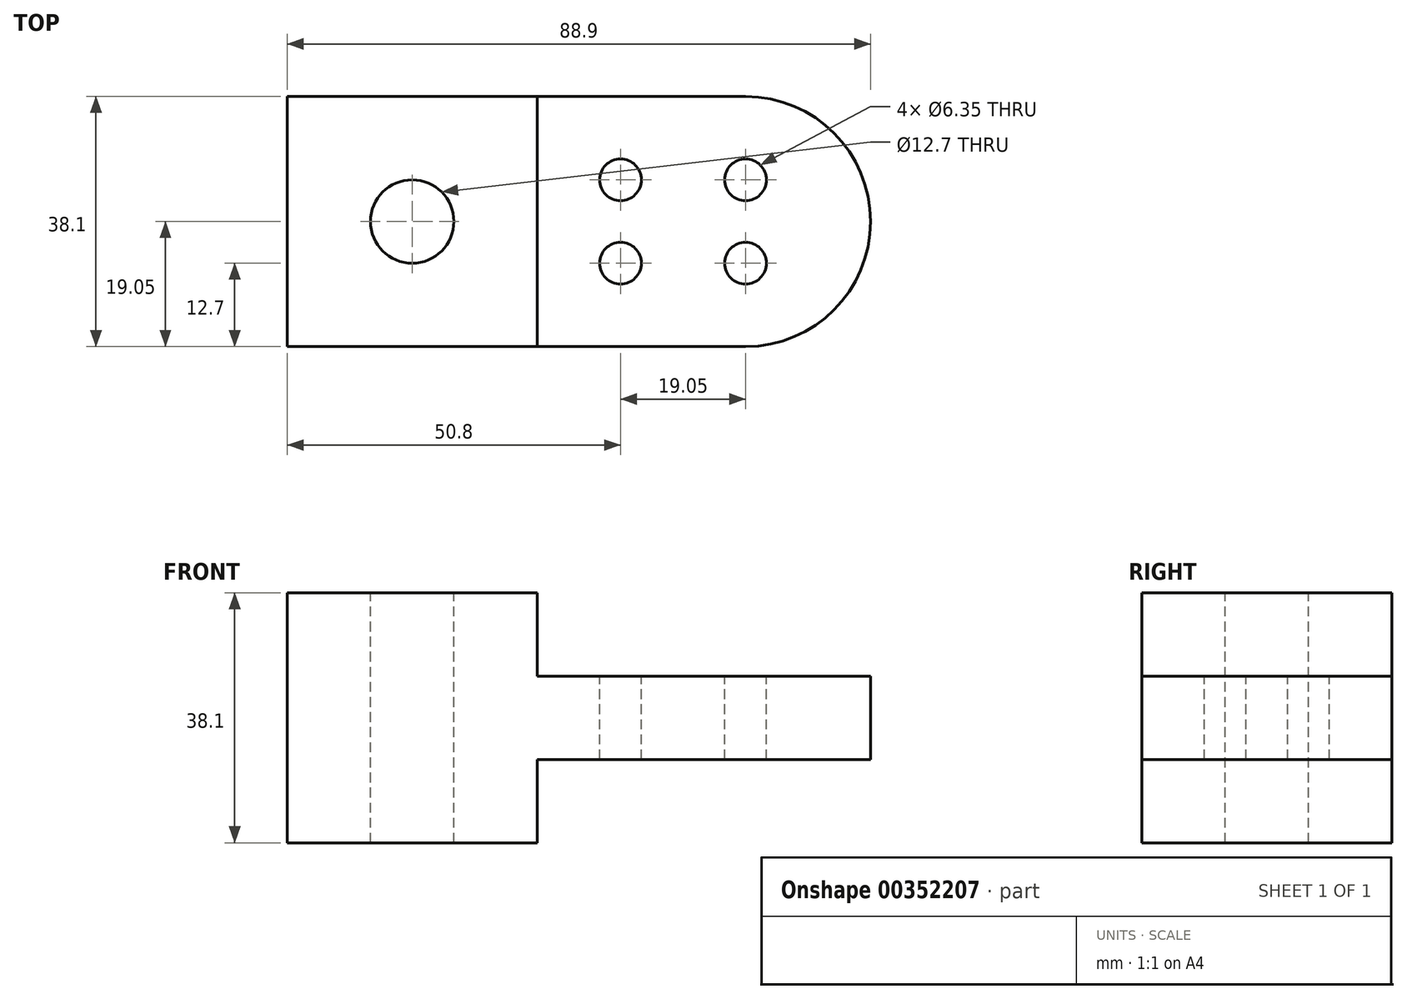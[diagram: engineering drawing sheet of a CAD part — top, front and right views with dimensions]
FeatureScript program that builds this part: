
annotation { "Feature Type Name" : "Feature", "Feature Type Description" : "" }
export const myFeature = defineFeature(function(context is Context, id is Id, definition is map)
    precondition{}
    {
        {
            var Q0;
            Q0=qCreatedBy(makeId("Front.planeOp"),FACE);
            var sketch = newSketch(context, id + "F0", { "sketchPlane" : qUnion([Q0])});
            skLineSegment(sketch, "E0.bottom", {"start": v(38.1, 38.1) * mm, "end": v(0, 38.1) * mm});
            skLineSegment(sketch, "E0.top", {"start": v(38.1, 0) * mm, "end": v(0, 0) * mm});
            skLineSegment(sketch, "E0.left", {"start": v(38.1, 38.1) * mm, "end": v(38.1, 0) * mm});
            skLineSegment(sketch, "E0.right", {"start": v(0, 38.1) * mm, "end": v(0, 0) * mm});
            skLineSegment(sketch, "E1", {"start": v(38.1, 25.4) * mm, "end": v(88.9, 25.4) * mm});
            skLineSegment(sketch, "E2", {"start": v(88.9, 25.4) * mm, "end": v(88.9, 12.7) * mm});
            skLineSegment(sketch, "E3", {"start": v(88.9, 12.7) * mm, "end": v(38.1, 12.7) * mm});
            skSolve(sketch);
        }
        {
            var Q0;
            Q0 = qSketchRegion(id + "F0", true);
            extrude(context, id + "F1", {"entities" : qUnion([Q0]), "endBound" : BoundingType.SYMMETRIC, "depth" : 38.1 * mm});
        }
        {
            var Q0;
            Q0=makeQuery(id+"F1.opExtrude","SWEPT_FACE",FACE,{"disambiguationData":[OSD([sQuery(id+"F0.wireOp",EDGE,"E1")])]});
            var sketch = newSketch(context, id + "F2", { "sketchPlane" : qUnion([Q0])});
            skLineSegment(sketch, "E4.0", {"start": v(38.1, 19.05) * mm, "end": v(69.85, 19.05) * mm});
            skLineSegment(sketch, "E5.0", {"start": v(38.1, -19.05) * mm, "end": v(69.85, -19.05) * mm});
            skArc(sketch, "E6", {"start": v(69.85, -19.05) * mm, "mid": v(88.9, 0) * mm, "end": v(69.85, 19.05) * mm});
            skPoint(sketch, "E7.orphan", {"position": v(88.9, 19.05) * mm});
            skPoint(sketch, "E8.0.start.orphan", {"position": v(88.9, -19.05) * mm});
            skLineSegment(sketch, "E9", {"start": v(38.1, 19.05) * mm, "end": v(85.46, 36.36) * mm});
            skLineSegment(sketch, "E10", {"start": v(85.46, 36.36) * mm, "end": v(102.93, 19.05) * mm});
            skLineSegment(sketch, "E11", {"start": v(102.93, 19.05) * mm, "end": v(98.11, -24.38) * mm});
            skLineSegment(sketch, "E12", {"start": v(98.11, -24.38) * mm, "end": v(40.89, -25.88) * mm});
            skLineSegment(sketch, "E13", {"start": v(40.89, -25.88) * mm, "end": v(38.1, -19.05) * mm});
            skSolve(sketch);
        }
        {
            var Q0;
            Q0 = qSketchRegion(id + "F2", true);
            extrude(context, id + "F3", {"entities" : qUnion([Q0]), "operationType" : NewBodyOperationType.REMOVE, "endBound" : BoundingType.THROUGH_ALL, "oppositeDirection" : true, "depth" : 25.4 * mm});
        }
        {
            var Q0;
            Q0=makeQuery(id+"F1.opExtrude","SWEPT_FACE",FACE,{"disambiguationData":[OSD([sQuery(id+"F0.wireOp",EDGE,"E1")])]});
            var sketch = newSketch(context, id + "F4", { "sketchPlane" : qUnion([Q0])});
            skLineSegment(sketch, "E14", {"start": v(0, 0) * mm, "end": v(76.76, 0) * mm, "construction": true});
            skCircle(sketch, "E15", {"center": v(50.8, 6.35) * mm, "radius": 3.18 * mm});
            skCircle(sketch, "E16", {"center": v(69.85, 6.35) * mm, "radius": 3.18 * mm});
            skCircle(sketch, "E17", {"center": v(69.85, -6.35) * mm, "radius": 3.18 * mm});
            skCircle(sketch, "E18", {"center": v(50.8, -6.35) * mm, "radius": 3.18 * mm});
            skSolve(sketch);
        }
        {
            var Q0;
            Q0 = qSketchRegion(id + "F4", true);
            extrude(context, id + "F5", {"entities" : qUnion([Q0]), "operationType" : NewBodyOperationType.REMOVE, "endBound" : BoundingType.THROUGH_ALL, "oppositeDirection" : true, "depth" : 25.4 * mm});
        }
        {
            var Q0;
            Q0=makeQuery(id+"F1.opExtrude","SWEPT_FACE",FACE,{"disambiguationData":[OSD([sQuery(id+"F0.wireOp",EDGE,"E0.bottom")])]});
            var sketch = newSketch(context, id + "F6", { "sketchPlane" : qUnion([Q0])});
            skCircle(sketch, "E19", {"center": v(19.05, 0) * mm, "radius": 6.35 * mm});
            skSolve(sketch);
        }
        {
            var Q0;
            Q0 = qSketchRegion(id + "F6", true);
            extrude(context, id + "F7", {"entities" : qUnion([Q0]), "operationType" : NewBodyOperationType.REMOVE, "endBound" : BoundingType.THROUGH_ALL, "oppositeDirection" : true, "depth" : 25.4 * mm});
        }
    });
